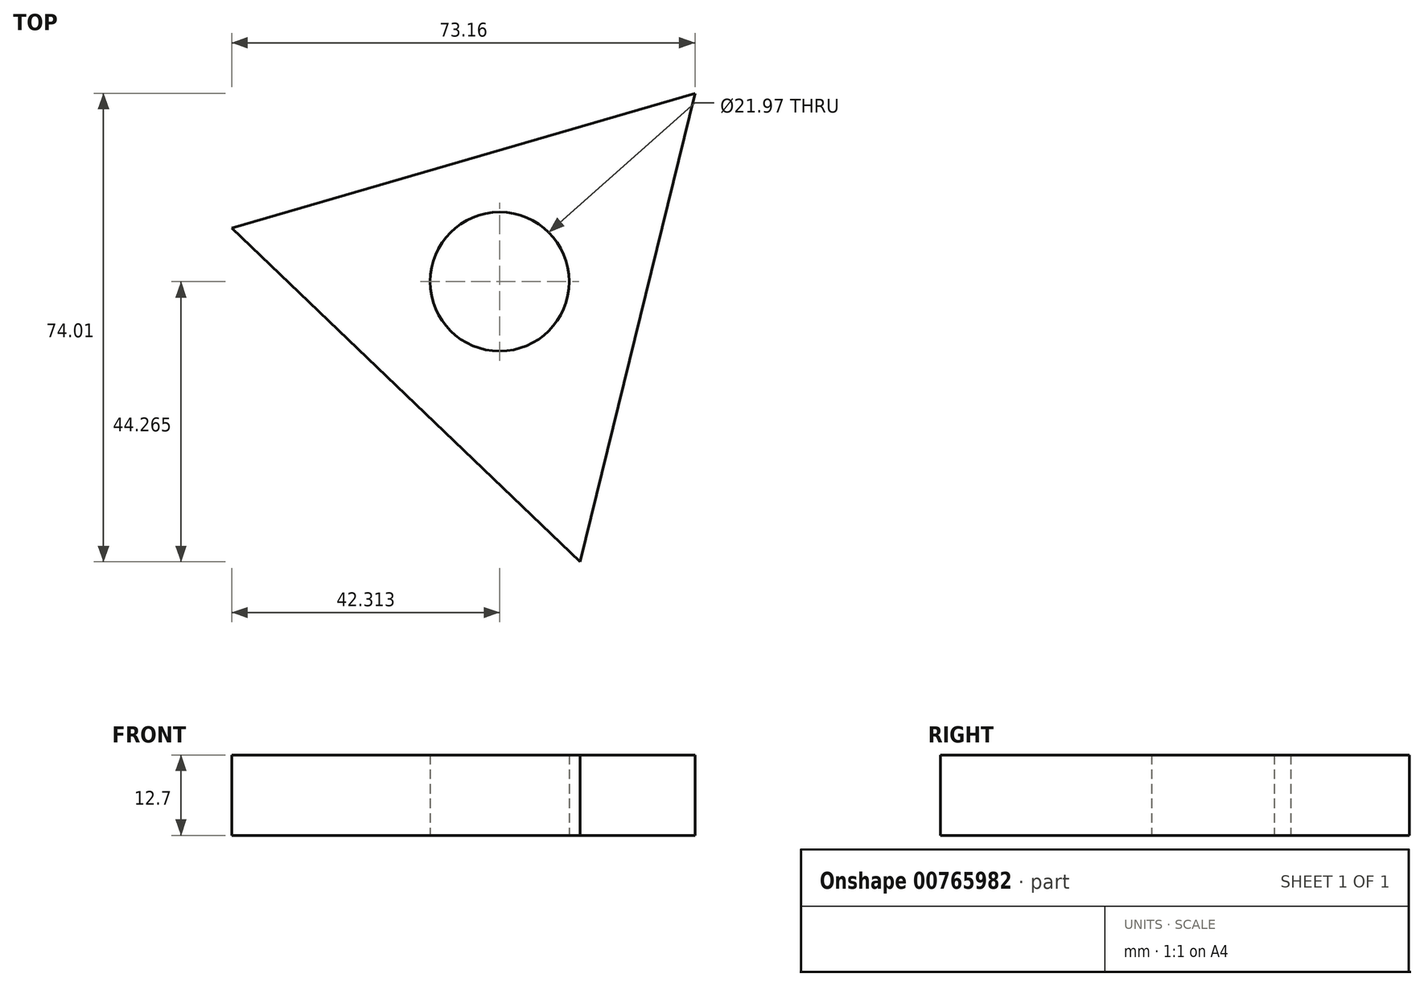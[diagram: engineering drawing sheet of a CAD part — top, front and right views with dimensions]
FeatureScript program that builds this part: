
annotation { "Feature Type Name" : "Feature", "Feature Type Description" : "" }
export const myFeature = defineFeature(function(context is Context, id is Id, definition is map)
    precondition{}
    {
        {
            var Q0;
            Q0=qCreatedBy(makeId("Top.planeOp"),FACE);
            var sketch = newSketch(context, id + "F0", { "sketchPlane" : qUnion([Q0])});
            skLineSegment(sketch, "E0.0", {"start": v(42.04, 50.29) * mm, "end": v(23.92, -23.72) * mm});
            skLineSegment(sketch, "E0.1", {"start": v(23.92, -23.72) * mm, "end": v(-31.12, 28.98) * mm});
            skLineSegment(sketch, "E0.2", {"start": v(-31.12, 28.98) * mm, "end": v(42.04, 50.29) * mm});
            skCircle(sketch, "E1", {"center": v(11.2, 20.54) * mm, "radius": 10.99 * mm});
            skSolve(sketch);
        }
        {
            var Q0;
            Q0 = qSketchRegion(id + "F0", true);
            extrude(context, id + "F1", {"entities" : qUnion([Q0]), "depth" : 12.7 * mm, "offsetDistance" : 25.4 * mm});
        }
    });
